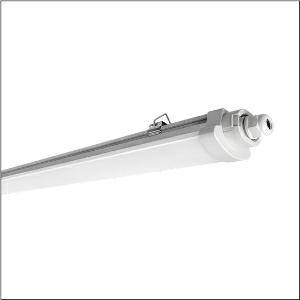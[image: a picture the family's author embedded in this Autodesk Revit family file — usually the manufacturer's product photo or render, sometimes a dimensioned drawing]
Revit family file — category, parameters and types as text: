
# Revit family: monsun_41_51fk20mk440a003
name_source: partatom
category: Lighting Fixtures
units: mm (PartAtom-declared; Revit-internal decimal feet)

## family parameters
Cut with Voids When Loaded = No
Host = Face
Light Source = No
Part Type = Normal
Room Calculation Point = No
Round Connector Dimension = Use Diameter
Shared = No

## types (1)
- --- (1 x LED, 4000 lm, 30 W, 4000K)
    Apparent Load = 30 VA
    CIE Flux Codes = 44 74 92 92 100
    Color Rendering = 80
    Color Temperature = 4000K
    Default Elevation = 1800 mm
    Description = Monsun 41, damp-proof luminaire, primary optical cover: diffuser, of PC, frosted, light emission: direct distribution, primary light characteristic: symmetric, installation type: surface-mounted, suspended mounting, LED, rated luminous flux: 4.000lm, luminous efficacy: 130lm/W, light colour: 840, colour temperature: 4000K, control gear: ON/OFF Multilumen, with terminal, 3-pole, through-wiring: 3x 1.5mm², mains connection: 220..240V, AC, 50/60Hz, rated input power: 30W, housing, luminaire housing, of PC, grey, length: 1.200mm, width: 79mm, height: 52mm, end cap, of PC, grey, ceiling mounting element, of stainless steel (V2A), protection rating (complete): IP65, insulation class (complete): insulation class II (safety insulation), certification: CE, UKCA, protection symbol: D, impact resistance: IK08, permissible operating ambient temperature: -20..+35°C, corresponds to IFS (International Featured Standards) requirements for safety and quality in the food industry, contact your sales advisor before using the luminaires in applications with unclear chemical exposure, large temperature fluctuations or condensation-forming humidity, packaging unit: 1 piece
    Height = 54 mm
    Lamp = 1 x LED
    Lamp Light Flux = 4000 lm
    Lamp Power = 30 W
    Lamp count = 1
    Length = 1200 mm
    Luminous efficacy = 133 lm/W
    Manufacturer = Siteco
    ModVariant = No
    Model = 51FK20MK440A003
    Mounting Place = Ceiling
    Mounting Type = Surface mounted
    Number of Poles = 1
    OnlyDefault = Yes
    Power Factor = 1
    Product Name = Monsun 41
    Product group = damp-proof luminaire
    ProductGroupID = 300
    Protection Class = Protection class II
    Protection Degree = IP 65
    RLX_Detail_Level = 1
    RLX_Emergency_Light_Flux = 0 lm
    RLX_Emergency_Type = 0
    RLX_Emergency_Type_DB = No
    RlxData = <blob elided: 32133 chars, md5=ee59f987>
    Socket = socket
    Standby Power = 0 W
    System Light Flux = 4000 lm
    System Power = 30 W
    Type Comments = factory setting: luminous flux: 100 % | (HIGH)
    Type Image = l_1007037.jpg
    URL = http://relux.com
    VarID = @adj_175739
    Voltage = 0 V
    Weight = 0.00 kg
    Width = 79 mm

## geometry (parser evidence)
native form markers: Blend x4, Sweep x13
no freeform markers — native parametric forms only
